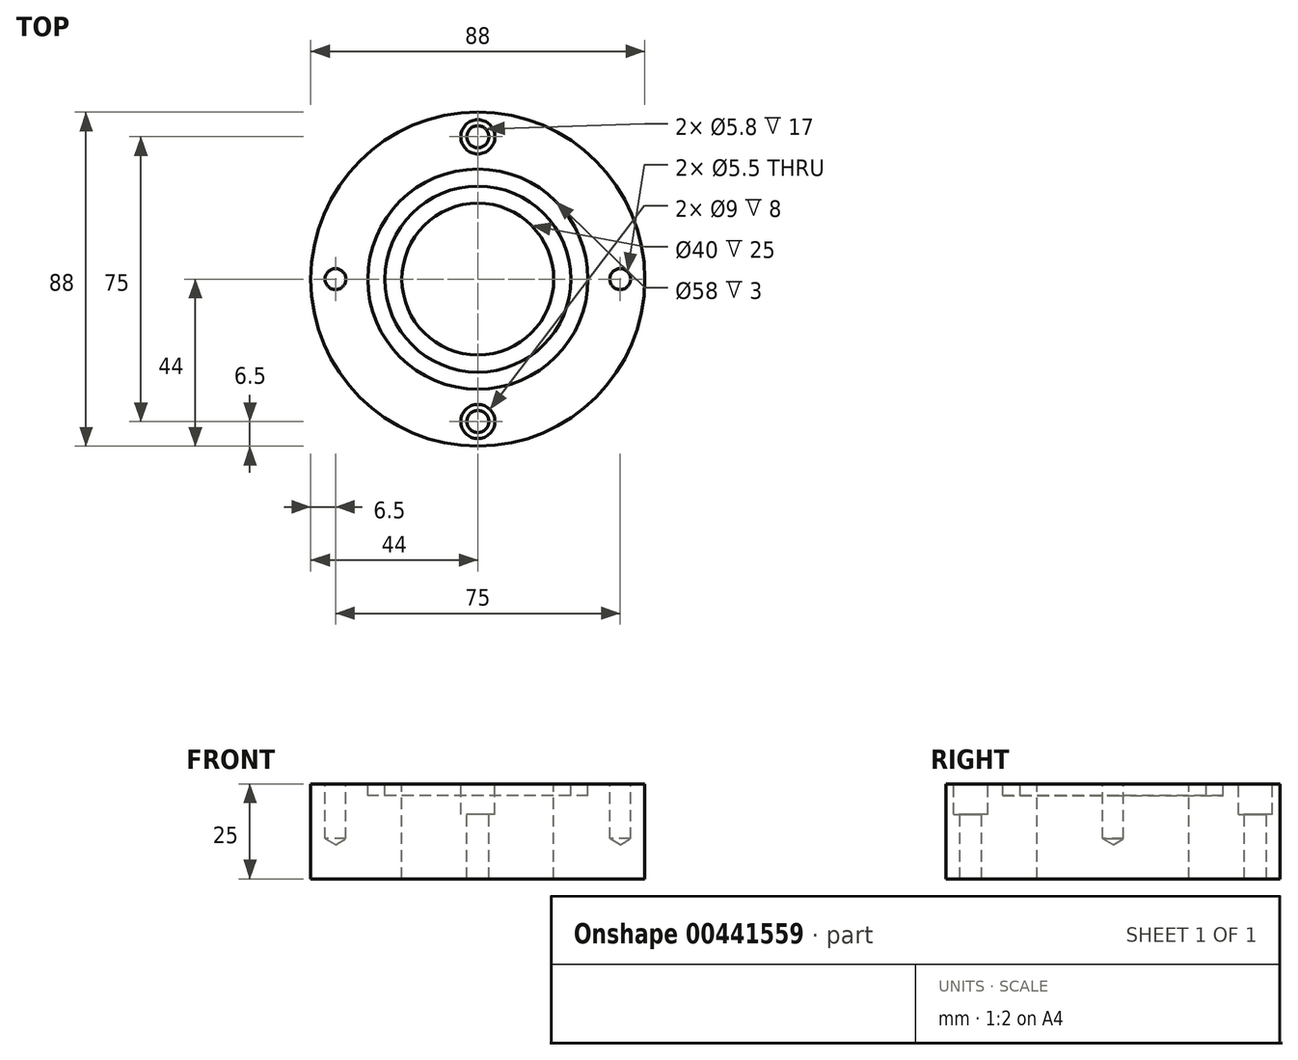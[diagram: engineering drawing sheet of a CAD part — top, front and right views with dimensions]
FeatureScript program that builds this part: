
annotation { "Feature Type Name" : "Feature", "Feature Type Description" : "" }
export const myFeature = defineFeature(function(context is Context, id is Id, definition is map)
    precondition{}
    {
        {
            var Q0;
            Q0=qCreatedBy(makeId("Front.planeOp"),FACE);
            var sketch = newSketch(context, id + "F0", { "sketchPlane" : qUnion([Q0])});
            skLineSegment(sketch, "E0", {"start": v(-20, 25) * mm, "end": v(-24.5, 25) * mm});
            skLineSegment(sketch, "E1", {"start": v(-44, 25) * mm, "end": v(-44, 17) * mm});
            skLineSegment(sketch, "E2", {"start": v(-44, 8) * mm, "end": v(-44, 0) * mm});
            skLineSegment(sketch, "E3", {"start": v(-44, 0) * mm, "end": v(-20, 0) * mm});
            skLineSegment(sketch, "E4", {"start": v(-20, 0) * mm, "end": v(-20, 25) * mm});
            skPoint(sketch, "E5.orphan", {"position": v(0, 25) * mm});
            skLineSegment(sketch, "E6", {"start": v(0, 25) * mm, "end": v(0, 0) * mm});
            skLineSegment(sketch, "E7", {"start": v(-24.5, 25) * mm, "end": v(-24.5, 22) * mm});
            skLineSegment(sketch, "E8", {"start": v(-24.5, 22) * mm, "end": v(-29, 22) * mm});
            skLineSegment(sketch, "E9", {"start": v(-29, 22) * mm, "end": v(-29, 25) * mm});
            skLineSegment(sketch, "E10.trimOffspring", {"start": v(-29, 25) * mm, "end": v(-44, 25) * mm});
            skLineSegment(sketch, "E11", {"start": v(-44, 17) * mm, "end": v(-44, 8) * mm});
            skPoint(sketch, "E12.start.orphan", {"position": v(-36, 25) * mm});
            skPoint(sketch, "E13.start.orphan", {"position": v(-33, 8) * mm});
            skSolve(sketch);
        }
        {
            var Q0;
            Q0=makeQuery(id+"F0.imprint","IMPRINT",FACE,{"disambiguationData":[TD([[makeQuery(id+"F0.imprint","IMPRINT",EDGE,{"derivedFrom":sQuery(id+"F0.wireOp",EDGE,"E0")}),1.0]])]});
            var Q1;
            Q1=sQuery(id+"F0.wireOp",EDGE,"E6");
            revolve(context, id + "F1", {"entities" : qUnion([Q0]), "axis" : qUnion([Q1]), "revolveType" : RevolveType.FULL});
        }
        {
            var Q0;
            Q0=makeQuery(id+"F1.opRevolve","SWEPT_FACE",FACE,{"disambiguationData":[OSD([sQuery(id+"F0.wireOp",EDGE,"E10.trimOffspring")])]});
            var sketch = newSketch(context, id + "F2", { "sketchPlane" : qUnion([Q0])});
            skPoint(sketch, "E14", {"position": v(0, 37.5) * mm});
            skPoint(sketch, "E15", {"position": v(0, -37.5) * mm});
            skSolve(sketch);
        }
        {
            var Q0;
            Q0=sQuery(id+"F2.wireOp",VERTEX,"E14");
            var Q1;
            Q1=sQuery(id+"F2.wireOp",VERTEX,"E15");
            var Q2;
            Q2=makeQuery(id+"F1.opRevolve","SWEPT_BODY",BODY,{"disambiguationData":[OSD([sQuery(id+"F0.wireOp",EDGE,"E0"),sQuery(id+"F0.wireOp",EDGE,"E1"),sQuery(id+"F0.wireOp",EDGE,"E2"),sQuery(id+"F0.wireOp",EDGE,"E3"),sQuery(id+"F0.wireOp",EDGE,"E4"),sQuery(id+"F0.wireOp",EDGE,"E7"),sQuery(id+"F0.wireOp",EDGE,"E8"),sQuery(id+"F0.wireOp",EDGE,"E9"),sQuery(id+"F0.wireOp",EDGE,"E10.trimOffspring"),sQuery(id+"F0.wireOp",EDGE,"E11")])]});
            hole(context, id + "F3", {"style" : HoleStyle.SIMPLE, "endStyle" : HoleEndStyle.BLIND, "holeDiameter" : 5.8 * mm, "holeDepth" : 40 * mm, "isTappedThrough" : true, "tappedDepth" : 12 * mm, "tapClearance" : 3, "locations" : qUnion([Q0, Q1]), "scope" : qUnion([Q2])});
        }
        {
            var Q0;
            Q0=makeQuery(id+"F1.opRevolve","SWEPT_FACE",FACE,{"disambiguationData":[OSD([sQuery(id+"F0.wireOp",EDGE,"E10.trimOffspring")])]});
            var sketch = newSketch(context, id + "F4", { "sketchPlane" : qUnion([Q0])});
            skPoint(sketch, "E16", {"position": v(-37.5, 0) * mm});
            skPoint(sketch, "E17", {"position": v(37.5, 0) * mm});
            skSolve(sketch);
        }
        {
            var Q0;
            Q0=sQuery(id+"F4.wireOp",VERTEX,"E16");
            var Q1;
            Q1=sQuery(id+"F4.wireOp",VERTEX,"E17");
            var Q2;
            Q2=makeQuery(id+"F1.opRevolve","SWEPT_BODY",BODY,{"disambiguationData":[OSD([sQuery(id+"F0.wireOp",EDGE,"E0"),sQuery(id+"F0.wireOp",EDGE,"E1"),sQuery(id+"F0.wireOp",EDGE,"E2"),sQuery(id+"F0.wireOp",EDGE,"E3"),sQuery(id+"F0.wireOp",EDGE,"E4"),sQuery(id+"F0.wireOp",EDGE,"E7"),sQuery(id+"F0.wireOp",EDGE,"E8"),sQuery(id+"F0.wireOp",EDGE,"E9"),sQuery(id+"F0.wireOp",EDGE,"E10.trimOffspring"),sQuery(id+"F0.wireOp",EDGE,"E11")])]});
            hole(context, id + "F5", {"style" : HoleStyle.SIMPLE, "endStyle" : HoleEndStyle.BLIND, "standardTappedOrClearance" : lookupTablePath({ "standard" : "ISO", "fit" : "Normal", "size" : "M5", "type" : "Clearance" }), "standardBlindInLast" : lookupTablePath({ "fit" : "Standard", "standard" : "ISO", "size" : "M5", "type" : "Clearance" }), "holeDiameter" : 5.5 * mm, "holeDepth" : 14.4 * mm, "isTappedThrough" : true, "tappedDepth" : 12 * mm, "tapClearance" : 3, "locations" : qUnion([Q0, Q1]), "scope" : qUnion([Q2])});
        }
        {
            var Q0;
            Q0=makeQuery(id+"F1.opRevolve","SWEPT_FACE",FACE,{"disambiguationData":[OSD([sQuery(id+"F0.wireOp",EDGE,"E10.trimOffspring")])]});
            var sketch = newSketch(context, id + "F6", { "sketchPlane" : qUnion([Q0])});
            skCircle(sketch, "E18.0", {"center": v(0, 37.5) * mm, "radius": 4.5 * mm});
            skCircle(sketch, "E19.0", {"center": v(0, -37.5) * mm, "radius": 4.5 * mm});
            skSolve(sketch);
        }
        {
            var Q0;
            Q0=makeQuery(id+"F6.imprint","IMPRINT",FACE,{"disambiguationData":[TD([[makeQuery(id+"F6.imprint","IMPRINT",EDGE,{"derivedFrom":sQuery(id+"F6.wireOp",EDGE,"E18.0")}),1.0]])]});
            var Q1;
            Q1=makeQuery(id+"F6.imprint","IMPRINT",FACE,{"disambiguationData":[TD([[makeQuery(id+"F6.imprint","IMPRINT",EDGE,{"derivedFrom":sQuery(id+"F6.wireOp",EDGE,"E19.0")}),1.0]])]});
            extrude(context, id + "F7", {"entities" : qUnion([Q0, Q1]), "operationType" : NewBodyOperationType.REMOVE, "oppositeDirection" : true, "depth" : 8 * mm});
        }
    });
